# Revit family: Blucher_PlumbingFixture_HygienicPro_IndustrialDrain1
name_source: partatom
category: Plumbing Fixtures
revit_build: Autodesk Revit 2017 (Build: 20190508_0315(x64)
units: mm (PartAtom-declared; Revit-internal decimal feet)

## family parameters
Cut with Voids When Loaded = No
Host = Face
OmniClass Number = 23.70.50.21.24
OmniClass Title = Waste Water Drains
Part Type = Normal
Room Calculation Point = No
Round Connector Dimension = Use Diameter
Shared = No

## types (1)
- FOR PRE-DEFINED TYPES PLEASE USE TYPE CATALOGUE
    Assembly Code = D2030300
    AssetType = Fixed
    BIMObjectName = Blucher_PlumbingFixture_HygienicPro
    CW Connection = No
    ClassificationName = Uniclass2015
    ClassificationValue = Pr_65_52_24_24
    Color = Stainless Steel
    CutoutThickess = 150 mm
    D = 110 mm  [stored 0.360892 ft]
    D1 = 160 mm  [stored 0.524934 ft]
    Default Elevation = 0 mm  [stored 0 ft]
    Description = Industrials drains for resin floors
    DocumentationCertificates = https://www.bimstore.co
    DocumentationInstallationGuide = https://www.bimstore.co
    DocumentationInstallationVideo = http://www.blucher.com
    DocumentationLiterature = https://www.bimstore.co
    DocumentationMaintenance = https://www.bimstore.co
    DocumentationTechnical = https://www.bimstore.co
    DrainProductCode = 790.273.000.60
    DrainType = HO : 756.573.110
    DrainType_755.503.110 = VO : 755.503.110
    DrainType_755.503.160 = VO : 755.503.160
    DrainType_755.513.110 = VO : 755.513.110
    DrainType_755.513.160 = VO : 755.513.160
    DrainType_755.573.110 = VO : 755.573.110
    DrainType_755.573.160 = VO : 755.573.160
    DrainType_756.503.110 = HO : 756.503.110
    DrainType_756.513.110 = HO : 756.513.110
    DrainType_756.573.110 = HO : 756.573.110
    DurationUnit = Years
    ExpectedLife = 50
    F = 305 mm  [stored 1.00066 ft]
    FilterBasketType = FB : N/A
    FilterBasket_780.004.010.05 = FB : 780.004.010.05
    FilterBasket_780.004.020.05 = FB : 780.004.020.05
    FilterBasket_780.004.030.05 = FB : 780.004.030.05
    Finish = 2B - Pickled
    Grade = AISI 304/EN 1.4301 or AISI 316L/EN 1.4404
    GratingType = G : 790.273.000.60
    GratingType_790.273.000.60 = G : 790.273.000.60
    H = 376 mm  [stored 1.2336 ft]
    H1 = 323 mm  [stored 1.05971 ft]
    H6 = 237 mm  [stored 0.777559 ft]
    HW Connection = No
    HeightFromLevel = 0 mm  [stored 0 ft]
    HorizontalOutletHeight = 58 mm
    HorizontalOutletLength = 153 mm  [stored 0.501969 ft]
    IfcExportAs = IfcFlowTerminal
    IfcExportType = IfcWasteTerminalTypeEnum.FLOORWASTE
    Keynote = R10
    Manufacturer = BLÜCHER
    ManufacturerName = BLÜCHER
    Material = Available in Stainless Steel AISI 304 & Stainless Steel AISI 316L
    Model = Hygienic Pro
    ModelReference = Hygienic Pro
    NBSDescription = Drainage channels with gratings
    NBSObjectName = BLÜCHER - Drainage channels with gratings
    NBSReference = 90-05-20/422
    NominalDepth = 305 mm  [stored 1.00066 ft]
    NominalHeight = 376 mm  [stored 1.2336 ft]
    NominalLength = 305 mm  [stored 1.00066 ft]
    OutletDiameter = 110 mm  [stored 0.360892 ft]
    ProductionYear = 2018
    ReferencedStandard = EN1253
    Shape = Rectangular
    Size = 660
    Type Comments = 755.513.110
    TypeName = 755.513.110
    URL = http://www.blucher.com
    Vent Connection = No
    W1 = 153 mm  [stored 0.501969 ft]
    WarrantyDurationUnit = Years
    Waste Connection = Yes
    WaterTrap_562.102.000 = WT : 562.102.000
    _BSBibleVersion = 15
    _BimSpecGuid = 0
    _CurrentRevision = 1
    _DistributedBy = www.bimstore.co.uk

note: [stored X ft] marks values corroborated as IEEE doubles in the binary element streams (Revit-internal decimal feet)

## geometry (parser evidence)
native form markers: Blend x4, Sweep x14
no freeform markers — native parametric forms only
